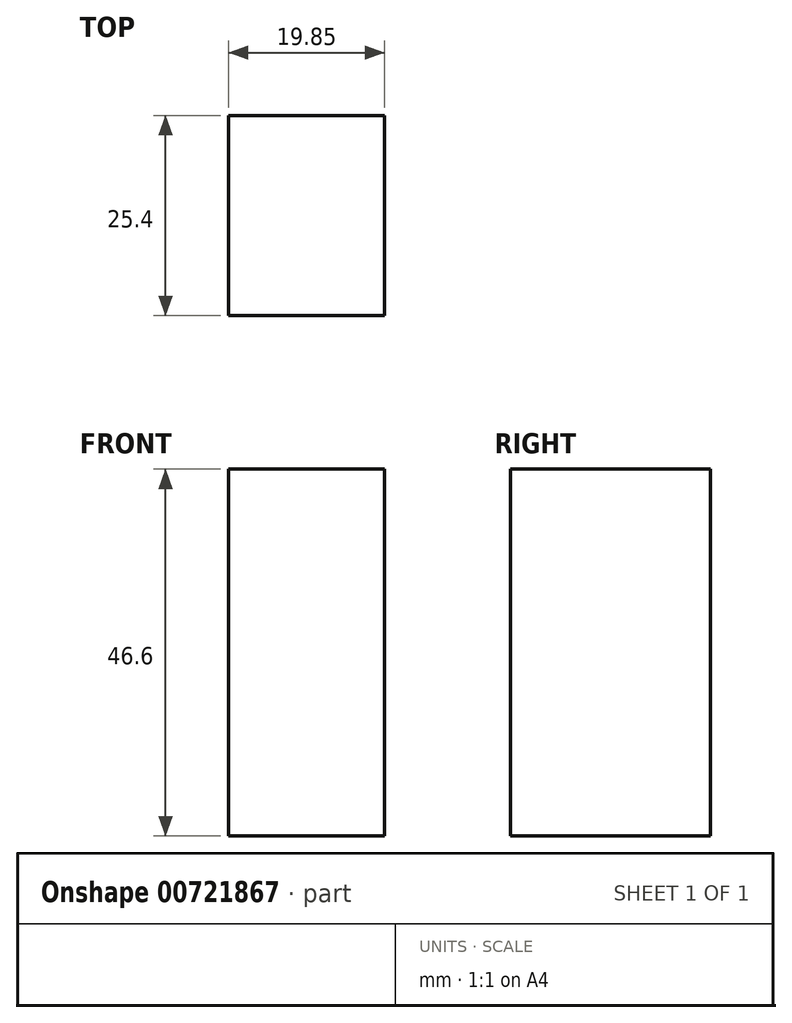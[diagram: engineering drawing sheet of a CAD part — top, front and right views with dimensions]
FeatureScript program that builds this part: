
annotation { "Feature Type Name" : "Feature", "Feature Type Description" : "" }
export const myFeature = defineFeature(function(context is Context, id is Id, definition is map)
    precondition{}
    {
        {
            var Q0;
            Q0=qCreatedBy(makeId("Front.planeOp"),FACE);
            var sketch = newSketch(context, id + "F0", { "sketchPlane" : qUnion([Q0])});
            skLineSegment(sketch, "E0.bottom", {"start": v(0, 0) * mm, "end": v(-19.85, 0) * mm});
            skLineSegment(sketch, "E0.top", {"start": v(0, 46.6) * mm, "end": v(-19.85, 46.6) * mm});
            skLineSegment(sketch, "E0.left", {"start": v(0, 0) * mm, "end": v(0, 46.6) * mm});
            skLineSegment(sketch, "E0.right", {"start": v(-19.85, 0) * mm, "end": v(-19.85, 46.6) * mm});
            skPoint(sketch, "E0.middle", {"position": v(-9.92, 23.3) * mm});
            skSolve(sketch);
        }
        {
            var Q0;
            Q0 = qSketchRegion(id + "F0", true);
            extrude(context, id + "F1", {"entities" : qUnion([Q0]), "endBound" : BoundingType.SYMMETRIC, "depth" : 25.4 * mm, "offsetDistance" : 25.4 * mm});
        }
    });
